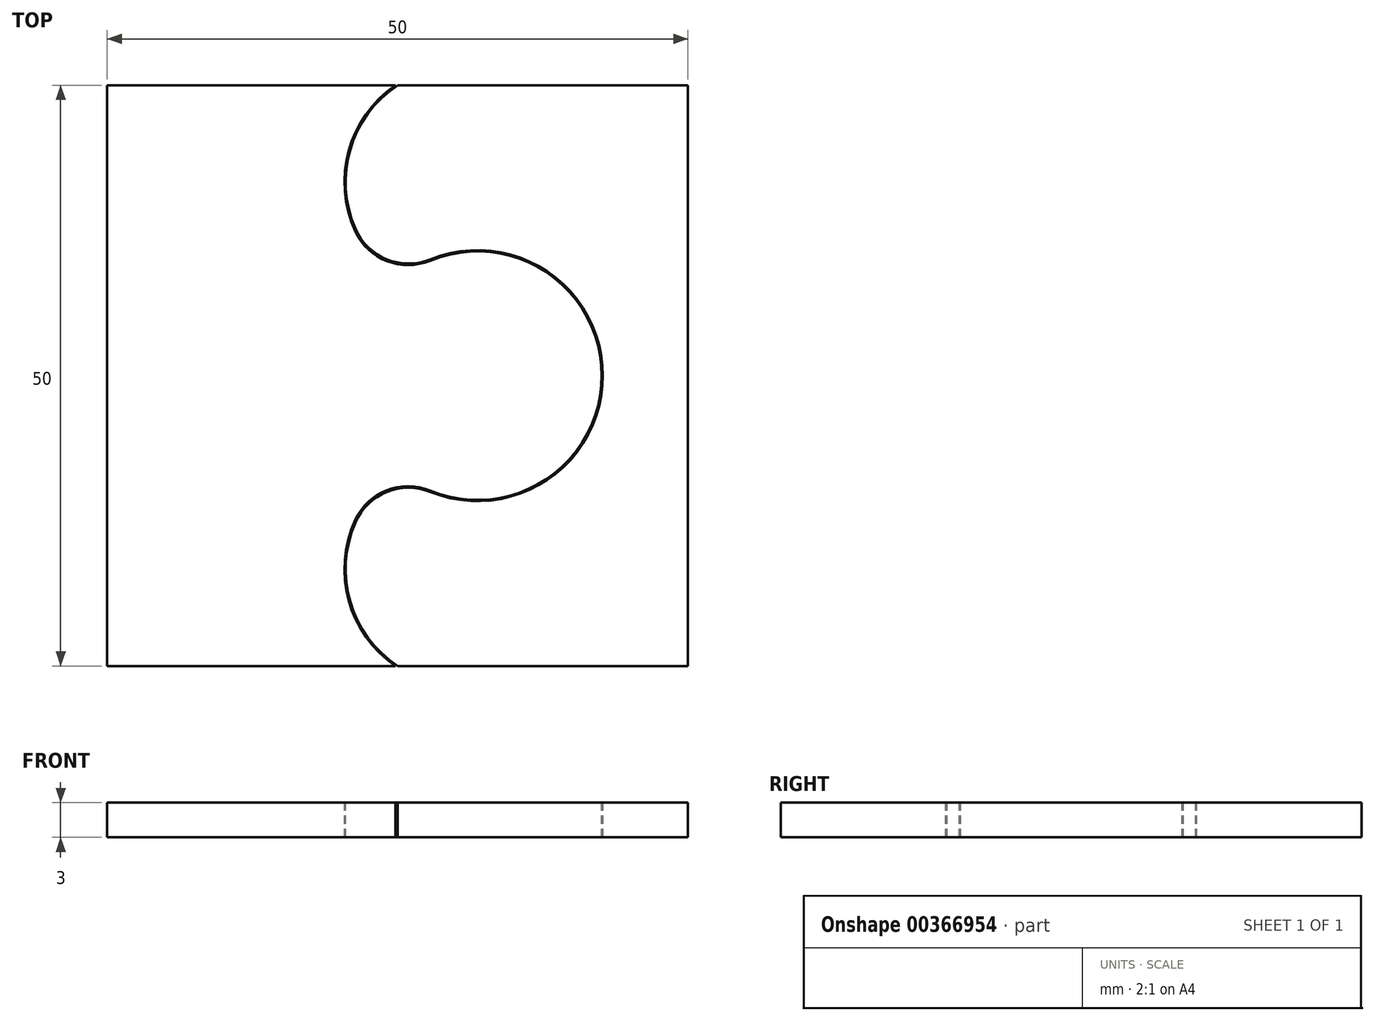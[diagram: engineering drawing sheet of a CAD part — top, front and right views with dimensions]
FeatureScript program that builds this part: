
annotation { "Feature Type Name" : "Feature", "Feature Type Description" : "" }
export const myFeature = defineFeature(function(context is Context, id is Id, definition is map)
    precondition{}
    {
        {
            var Q0;
            Q0=qCreatedBy(makeId("Top.planeOp"),FACE);
            var sketch = newSketch(context, id + "F0", { "sketchPlane" : qUnion([Q0])});
            skLineSegment(sketch, "E0.bottom", {"start": v(-46.91, 11.77) * mm, "end": v(3.09, 11.77) * mm});
            skLineSegment(sketch, "E0.top", {"start": v(-46.91, -38.23) * mm, "end": v(3.09, -38.23) * mm});
            skLineSegment(sketch, "E0.left", {"start": v(-46.91, 11.77) * mm, "end": v(-46.91, -38.23) * mm});
            skLineSegment(sketch, "E0.right", {"start": v(3.09, 11.77) * mm, "end": v(3.09, -38.23) * mm});
            skSolve(sketch);
        }
        {
            var Q0;
            Q0=makeQuery(id+"F0.imprint","IMPRINT",FACE,{"disambiguationData":[TD([[makeQuery(id+"F0.imprint","IMPRINT",EDGE,{"derivedFrom":sQuery(id+"F0.wireOp",EDGE,"E0.bottom")}),-1.0]])]});
            extrude(context, id + "F1", {"entities" : qUnion([Q0]), "depth" : 3 * mm});
        }
        {
            var Q0;
            Q0=makeQuery(id+"F1.opExtrude","CAP_FACE",FACE,{"disambiguationData":[OSD([sQuery(id+"F0.wireOp",EDGE,"E0.bottom"),sQuery(id+"F0.wireOp",EDGE,"E0.top"),sQuery(id+"F0.wireOp",EDGE,"E0.left"),sQuery(id+"F0.wireOp",EDGE,"E0.right")])],"isStart":false});
            var sketch = newSketch(context, id + "F2", { "sketchPlane" : qUnion([Q0])});
            skLineSegment(sketch, "E1", {"start": v(-21.91, -21.56) * mm, "end": v(-21.91, -38.23) * mm, "construction": true});
            skLineSegment(sketch, "E2", {"start": v(-21.91, 11.77) * mm, "end": v(-21.91, -4.9) * mm, "construction": true});
            skLineSegment(sketch, "E3", {"start": v(-21.91, -4.9) * mm, "end": v(-21.91, -21.56) * mm, "construction": true});
            skArc(sketch, "E4", {"start": v(-21.91, 11.77) * mm, "mid": v(-25.98, 6.25) * mm, "end": v(-25.53, -0.6) * mm});
            skArc(sketch, "E5", {"start": v(-19.08, -23.24) * mm, "mid": v(-4.23, -13.23) * mm, "end": v(-19.08, -3.21) * mm});
            skArc(sketch, "E6", {"start": v(-25.53, -25.86) * mm, "mid": v(-25.98, -32.7) * mm, "end": v(-21.91, -38.23) * mm});
            skArc(sketch, "E7.0", {"start": v(-25.55, -25.65) * mm, "mid": v(-26.1, -32.64) * mm, "end": v(-21.97, -38.31) * mm});
            skArc(sketch, "E7.1", {"start": v(-19.1, -23.13) * mm, "mid": v(-4.33, -13.23) * mm, "end": v(-19.1, -3.33) * mm});
            skArc(sketch, "E7.2", {"start": v(-21.97, 11.86) * mm, "mid": v(-26.1, 6.19) * mm, "end": v(-25.55, -0.8) * mm});
            skLineSegment(sketch, "E8", {"start": v(-21.97, 11.86) * mm, "end": v(-21.91, 11.77) * mm});
            skLineSegment(sketch, "E9", {"start": v(-21.97, -38.31) * mm, "end": v(-21.91, -38.23) * mm});
            skPoint(sketch, "E10.visualSharp", {"position": v(-21.9, -5.02) * mm});
            skArc(sketch, "E10.filletArc", {"start": v(-25.55, -0.8) * mm, "mid": v(-22.83, -3.36) * mm, "end": v(-19.1, -3.33) * mm});
            skPoint(sketch, "E11.visualSharp", {"position": v(-21.91, -4.9) * mm});
            skArc(sketch, "E11.filletArc", {"start": v(-25.53, -0.6) * mm, "mid": v(-22.84, -3.2) * mm, "end": v(-19.08, -3.21) * mm});
            skPoint(sketch, "E12.visualSharp", {"position": v(-21.9, -21.44) * mm});
            skArc(sketch, "E12.filletArc", {"start": v(-19.1, -23.13) * mm, "mid": v(-22.83, -23.1) * mm, "end": v(-25.55, -25.65) * mm});
            skPoint(sketch, "E13.visualSharp", {"position": v(-21.91, -21.56) * mm});
            skArc(sketch, "E13.filletArc", {"start": v(-19.08, -23.24) * mm, "mid": v(-22.84, -23.25) * mm, "end": v(-25.53, -25.86) * mm});
            skSolve(sketch);
        }
        {
            var Q0;
            {var subQ4=sQuery(id+"F2.wireOp",EDGE,"E4");Q0=makeQuery(id+"F2.imprint","IMPRINT",FACE,{"disambiguationData":[TD([[makeQuery(id+"F2.imprint","IMPRINT",EDGE,{"derivedFrom":subQ4}),-1.0]])]});}
            extrude(context, id + "F3", {"entities" : qUnion([Q0]), "operationType" : NewBodyOperationType.REMOVE, "oppositeDirection" : true, "depth" : 25 * mm});
        }
    });
